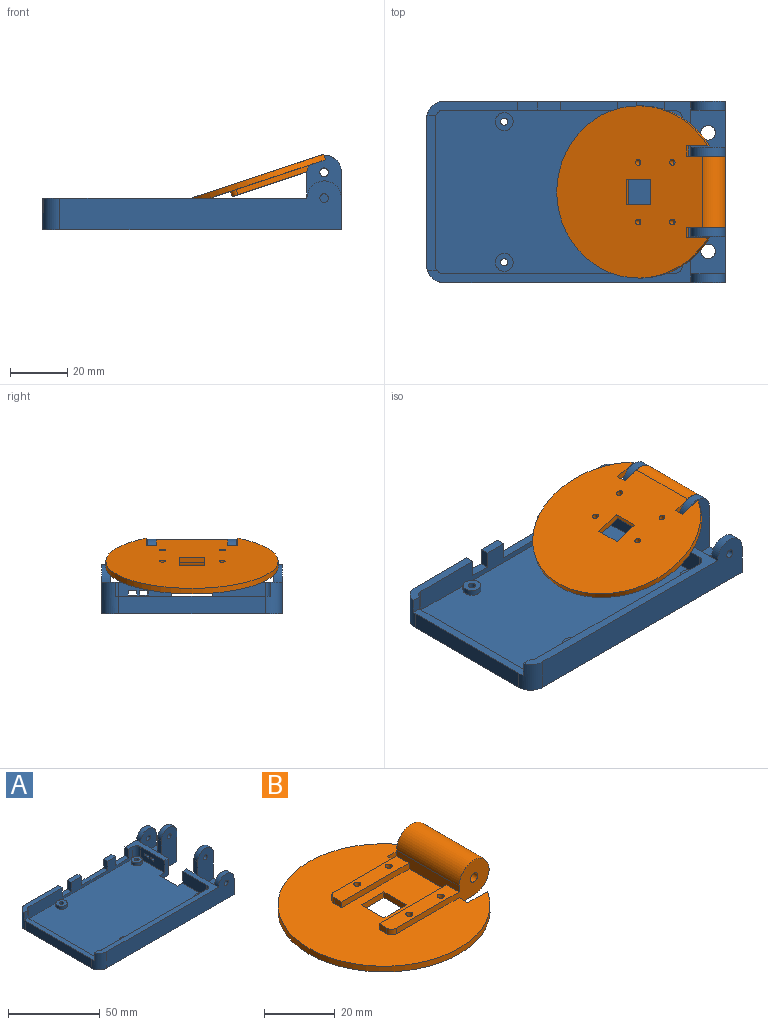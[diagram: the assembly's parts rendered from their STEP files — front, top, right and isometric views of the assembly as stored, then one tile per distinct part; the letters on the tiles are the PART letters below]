
ASSEMBLY  parts=2 mates=1
PART A: 83 faces, bbox 104x63x26 mm
  f0: plane 13x8mm, normal (1,0,0), area 104mm2, adj f3,f16,f69,f78
  f1: plane 13x12mm, normal (0,0,1), area 135.7mm2, adj f4,f65,f66,f72,f77
  f2: plane 11x5.5mm, normal (1,0,0), area 60.5mm2, adj f7,f18,f60,f64
  f3: plane 13x12mm, normal (0,0,1), area 135.7mm2, adj f0,f63,f67,f69,f78
  f4: plane 13x8mm, normal (1,0,0), area 95.4mm2, adj f1,f7,f51,f52,f54,f55,f56,f57
  f5: plane 11x5.5mm, normal (1,0,0), area 60.5mm2, adj f16,f18,f59,f62
  f6: plane 86x57mm, normal (0,0,1), area 4718mm2, adj f8,f13,f15,f17,f20,f21,f23,f25
  f7: plane 24.5x9.1mm, normal (0,0,1), area 93.6mm2, adj f2,f4,f8,f12,f13,f34,f49,f60
  f8: plane 18.6x8mm, normal (-1,0,0), area 139.8mm2, adj f6,f7,f34,f51,f52,f53,f54,f55
  f9: plane 6.4x3mm, normal (0,0,1), area 19.2mm2, adj f12,f13,f45,f50
  f10: plane 8x3mm, normal (0,0,1), area 24mm2, adj f12,f13,f42,f46
  f11: plane 31.42x5mm, normal (0,0,1), area 94.6mm2, adj f12,f13,f35,f38,f41,f43
  f12: plane 98x17mm, normal (0,1,0), area 905.5mm2, adj f7,f9,f10,f11,f18,f38,f42,f43
  f13: plane 80.2x8mm, normal (0,-1,0), area 419.6mm2, adj f6,f7,f9,f10,f11,f34,f35,f42
  f14: plane 51x6mm, normal (-1,0,0), area 306mm2, adj f18,f37,f38,f40
  f15: plane 51.2x3mm, normal (1,0,0), area 153.6mm2, adj f6,f17,f35,f40
  f16: plane 91.66x24.5mm, normal (0,0,1), area 339.2mm2, adj f0,f5,f17,f19,f20,f21,f36,f37
  f17: cylinder r=2.9mm len=8mm, axis (0,0,1), area 26.1mm2, adj f6,f15,f16,f20,f39,f40
  f18: plane 104x63mm, normal (0,0,-1), area 6078.4mm2, adj f2,f5,f12,f14,f19,f30,f31,f32
  f19: plane 98x17mm, normal (0,-1,0), area 1127.5mm2, adj f16,f18,f37,f63,f80,f81
  f20: plane 80.2x8mm, normal (0,1,0), area 641.6mm2, adj f6,f16,f17,f36
  f21: plane 18.6x8mm, normal (-1,0,0), area 148.8mm2, adj f6,f16,f36,f59
  f22: plane 6.2x6.2mm, normal (0,0,1), area 25.3mm2, adj f23,f33
  f23: cylinder r=3.1mm len=6.2mm, axis (0,0,1), area 39mm2, adj f6,f22
  f24: plane 6.2x6.2mm, normal (0,0,1), area 25.3mm2, adj f25,f32
  f25: cylinder r=3.1mm len=6.2mm, axis (0,0,1), area 39mm2, adj f6,f24
  f26: plane 6.2x6.2mm, normal (0,0,1), area 25.3mm2, adj f27,f31
  f27: cylinder r=3.1mm len=6.2mm, axis (0,0,1), area 39mm2, adj f6,f26
  f28: plane 6.2x6.2mm, normal (0,0,1), area 25.3mm2, adj f29,f30
  f29: cylinder r=3.1mm len=6.2mm, axis (0,0,1), area 39mm2, adj f6,f28
  f30: cylinder r=1.25mm len=5mm, axis (0,0,1), area 39.3mm2, adj f18,f28
  f31: cylinder r=1.25mm len=5mm, axis (0,0,1), area 39.3mm2, adj f18,f26
  f32: cylinder r=1.25mm len=5mm, axis (0,0,1), area 39.3mm2, adj f18,f24
  f33: cylinder r=1.25mm len=5mm, axis (0,0,1), area 39.3mm2, adj f18,f22
  f34: cylinder r=2.9mm len=8mm, axis (0,0,1), area 36.4mm2, adj f6,f7,f8,f13
  f35: cylinder r=2.9mm len=8mm, axis (0,0,-1), area 31.9mm2, adj f6,f11,f13,f15,f40,f41
  f36: cylinder r=2.9mm len=8mm, axis (0,0,-1), area 36.4mm2, adj f6,f16,f20,f21
  f37: cylinder r=6mm len=11mm, axis (0,0,-1), area 93.5mm2, adj f14,f16,f18,f19,f39,f40
  f38: cylinder r=6mm len=11mm, axis (0,0,1), area 98.6mm2, adj f11,f12,f14,f18,f40,f41
  f39: plane 5x3.37mm, normal (0,1,0), area 16.8mm2, adj f16,f17,f37,f40
  f40: plane 54x3.71mm, normal (0,0,1), area 162.2mm2, adj f14,f15,f17,f35,f37,f38,f39,f41
  f41: plane 5x3.06mm, normal (0,-1,0), area 15.3mm2, adj f11,f35,f38,f40
  f42: plane 6x3mm, normal (-1,0,0), area 18mm2, adj f10,f12,f13,f44
  f43: plane 6x3mm, normal (1,0,0), area 18mm2, adj f11,f12,f13,f44
  f44: plane 7x3mm, normal (0,0,1), area 21mm2, adj f12,f13,f42,f43
  f45: plane 6x3mm, normal (-1,0,0), area 18mm2, adj f9,f12,f13,f47
  f46: plane 6x3mm, normal (1,0,0), area 18mm2, adj f10,f12,f13,f47
  f47: plane 20x3mm, normal (0,0,1), area 60mm2, adj f12,f13,f45,f46
  f48: plane 10x3mm, normal (0,0,1), area 30mm2, adj f12,f13,f49,f50
  f49: plane 6x3mm, normal (-1,0,0), area 18mm2, adj f7,f12,f13,f48
  f50: plane 6x3mm, normal (1,0,0), area 18mm2, adj f9,f12,f13,f48
  f51: plane 3x3mm, normal (0,0,-1), area 9mm2, adj f4,f8,f52,f53,f71
  f52: plane 3x1.5mm, normal (0,-1,0), area 4.5mm2, adj f4,f8,f51,f54
  f53: plane 3x1.5mm, normal (0,1,0), area 4.5mm2, adj f8,f51,f54,f71
  f54: plane 3x3mm, normal (0,0,1), area 9mm2, adj f4,f8,f52,f53,f71
  f55: plane 3x3mm, normal (0,0,-1), area 9mm2, adj f4,f8,f56,f57
  f56: plane 3x1.5mm, normal (0,-1,0), area 4.5mm2, adj f4,f8,f55,f58
  f57: plane 3x1.5mm, normal (0,1,0), area 4.5mm2, adj f4,f8,f55,f58
  f58: plane 3x3mm, normal (0,0,1), area 9mm2, adj f4,f8,f56,f57
  f59: plane 11x7mm, normal (0,1,0), area 45mm2, adj f5,f6,f16,f18,f21,f61
  f60: plane 11x7mm, normal (0,-1,0), area 45mm2, adj f2,f6,f7,f8,f18,f61
  f61: plane 14x3mm, normal (1,0,0), area 42mm2, adj f6,f18,f59,f60
  f62: plane 26x12mm, normal (0,1,0), area 289.5mm2, adj f5,f18,f63,f68,f74,f76
  f63: plane 20x19mm, normal (1,0,0), area 132mm2, adj f3,f18,f19,f62,f69,f74,f78,f80
  f64: plane 26x12mm, normal (0,-1,0), area 289.5mm2, adj f2,f18,f65,f70,f73,f75
  f65: plane 20x19mm, normal (1,0,0), area 132mm2, adj f1,f12,f18,f64,f72,f73,f77,f79
  f66: cylinder r=2.54mm len=5.08mm, axis (0,0,1), area 47.9mm2, adj f1,f18
  f67: cylinder r=2.54mm len=5.08mm, axis (0,0,1), area 47.9mm2, adj f3,f18
  f68: plane 9x3mm, normal (-1,0,0), area 27mm2, adj f16,f62,f69,f74
  f69: plane 23x12mm, normal (0,-1,0), area 253.5mm2, adj f0,f3,f63,f68,f74,f76
  f70: plane 9x3mm, normal (-1,0,0), area 27mm2, adj f7,f64,f72,f73
  f71: plane 1.5x0.25mm, normal (-1,0,0), area 0.4mm2, adj f51,f53,f54,f72
  f72: plane 23x12mm, normal (0,1,0), area 253.5mm2, adj f1,f4,f65,f70,f71,f73,f75
  f73: cylinder r=6mm len=12mm, axis (0,-1,0), area 56.5mm2, adj f64,f65,f70,f72
  f74: cylinder r=6mm len=12mm, axis (0,-1,0), area 56.5mm2, adj f62,f63,f68,f69
  f75: cylinder r=1.5mm len=3mm, axis (0,-1,0), area 28.3mm2, adj f64,f72
  f76: cylinder r=1.5mm len=3mm, axis (0,-1,0), area 28.3mm2, adj f62,f69
  f77: plane 14x12mm, normal (0,-1,0), area 145.5mm2, adj f1,f4,f65,f79,f82
  f78: plane 14x12mm, normal (0,1,0), area 145.5mm2, adj f0,f3,f63,f80,f81
  f79: cylinder r=6mm len=12mm, axis (0,1,0), area 56.5mm2, adj f7,f12,f65,f77
  f80: cylinder r=6mm len=12mm, axis (0,1,0), area 56.5mm2, adj f16,f19,f63,f78
  f81: cylinder r=1.5mm len=3mm, axis (0,-1,0), area 28.3mm2, adj f19,f78
  f82: cylinder r=1.5mm len=3mm, axis (0,1,0), area 28.3mm2, adj f12,f77
PART B: 28 faces, bbox 59.5x60x12 mm
  f0: plane 3x2mm, normal (-1,0,0), area 6mm2, adj f2,f10,f21,f22
  f1: plane 37x12mm, normal (0,1,0), area 163.8mm2, adj f2,f3,f4,f6,f7,f9,f20,f23
  f2: plane 60x55.38mm, normal (0,0,1), area 2127mm2, adj f0,f1,f4,f5,f8,f9,f10,f11
  f3: plane 60x55.38mm, normal (0,0,-1), area 2532.8mm2, adj f1,f7,f8,f11,f12,f13,f14,f15
  f4: plane 25x4mm, normal (-1,0,0), area 80mm2, adj f1,f2,f7,f8,f19,f20,f21,f22
  f5: plane 3x2mm, normal (-1,0,0), area 6mm2, adj f2,f9,f19,f20
  f6: cylinder r=1.5mm len=25mm, axis (0,1,0), area 235.6mm2, adj f1,f8
  f7: cylinder r=6mm len=25mm, axis (0,1,0), area 706.9mm2, adj f1,f3,f4,f8
  f8: plane 37x12mm, normal (0,-1,0), area 163.8mm2, adj f2,f3,f4,f6,f7,f10,f22,f24
  f9: cylinder r=2mm len=2mm, axis (0,0,-1), area 6.3mm2, adj f1,f2,f5,f20
  f10: cylinder r=2mm len=2mm, axis (0,0,1), area 6.3mm2, adj f0,f2,f8,f22
  f11: plane 9x2mm, normal (-1,0,0), area 18mm2, adj f2,f3,f12,f13
  f12: plane 9x2mm, normal (0,1,0), area 18mm2, adj f2,f3,f11,f14
  f13: plane 9x2mm, normal (0,-1,0), area 18mm2, adj f2,f3,f11,f14
  f14: plane 9x2mm, normal (1,0,0), area 18mm2, adj f2,f3,f12,f13
  f15: cylinder r=1mm len=4mm, axis (0,0,1), area 25.1mm2, adj f3,f20
  f16: cylinder r=1mm len=4mm, axis (0,0,1), area 25.1mm2, adj f3,f20
  f17: cylinder r=1mm len=4mm, axis (0,0,1), area 25.1mm2, adj f3,f22
  f18: cylinder r=1mm len=4mm, axis (0,0,1), area 25.1mm2, adj f3,f22
  f19: plane 27x2mm, normal (0,-1,0), area 54mm2, adj f2,f4,f5,f20
  f20: plane 27x5mm, normal (0,0,1), area 127.9mm2, adj f1,f4,f5,f9,f15,f16,f19
  f21: plane 27x2mm, normal (0,1,0), area 54mm2, adj f0,f2,f4,f22
  f22: plane 27x5mm, normal (0,0,1), area 127.9mm2, adj f0,f4,f8,f10,f17,f18,f21
  f23: plane 3.5x2mm, normal (1,0,0), area 7mm2, adj f1,f2,f3,f27
  f24: plane 3.5x2mm, normal (1,0,0), area 7mm2, adj f2,f3,f8,f25
  f25: plane 7.84x2mm, normal (0,1,0), area 15.7mm2, adj f2,f3,f24,f26
  f26: cylinder r=30mm len=60mm, axis (0,0,-1), area 309.5mm2, adj f2,f3,f25,f27
  f27: plane 7.84x2mm, normal (0,-1,0), area 15.7mm2, adj f2,f3,f23,f26
PLACE A at identity fixed
PLACE B rot(axis=(0.99,0,0.16),180deg) t=(52,0,20)mm
MATE revolute A.f74 <-> B.f6  axis (0,-1,0) through (52,12.5,20)mm
